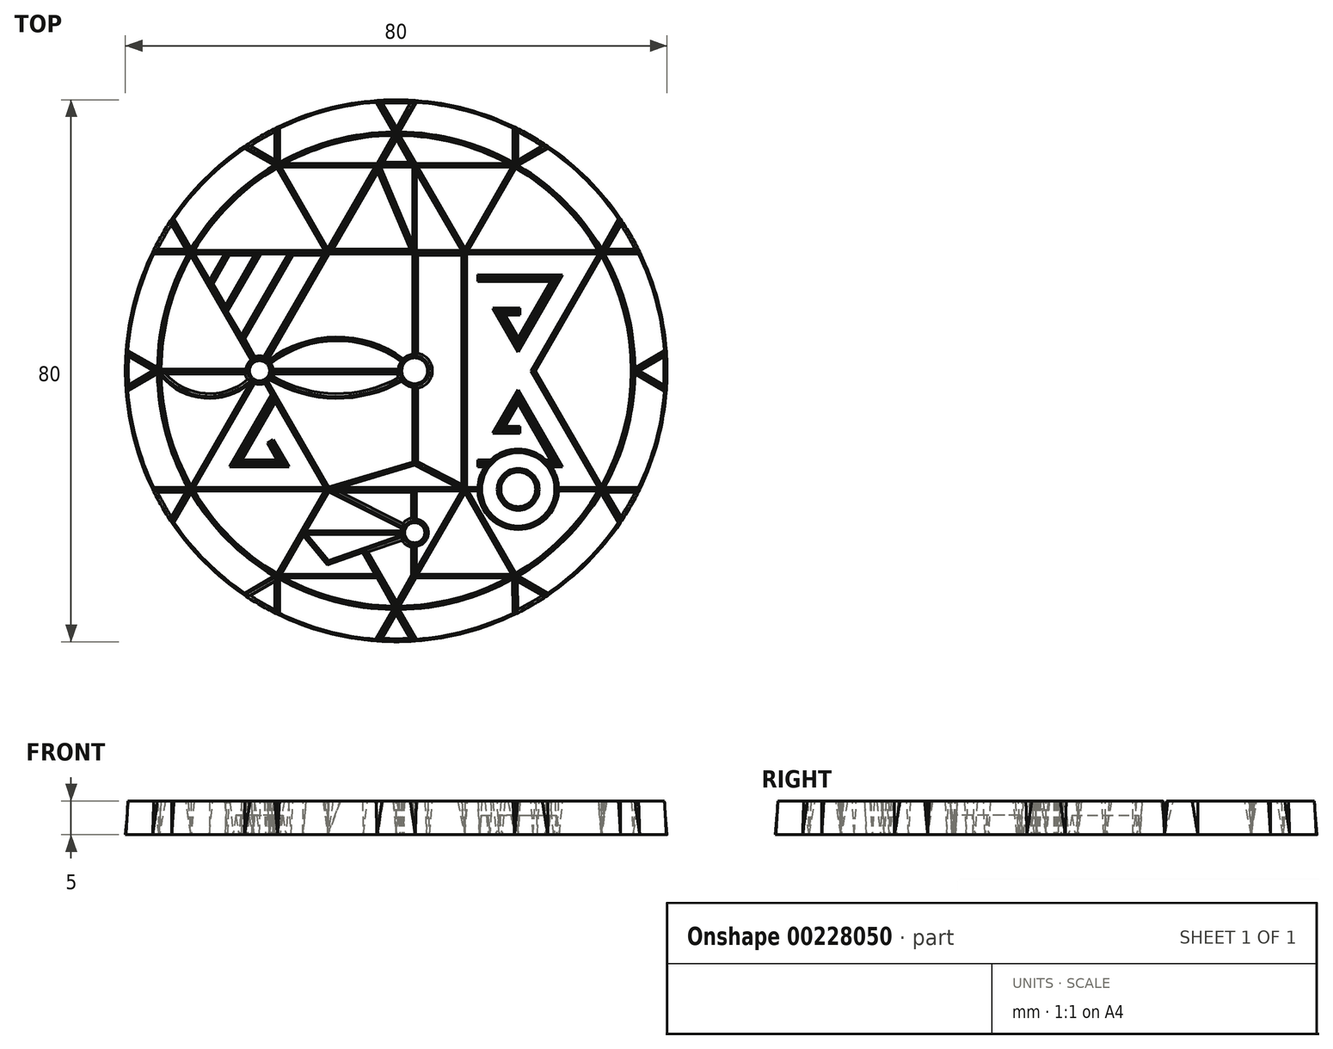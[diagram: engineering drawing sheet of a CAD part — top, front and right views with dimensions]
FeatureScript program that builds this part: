
annotation { "Feature Type Name" : "Feature", "Feature Type Description" : "" }
export const myFeature = defineFeature(function(context is Context, id is Id, definition is map)
    precondition{}
    {
        {
            var Q0;
            Q0=qCreatedBy(makeId("Top.planeOp"),FACE);
            var sketch = newSketch(context, id + "F6", { "sketchPlane" : qUnion([Q0])});
            skCircle(sketch, "E0", {"center": v(0, 0) * mm, "radius": 40 * mm});
            skCircle(sketch, "E1", {"center": v(0, 0) * mm, "radius": 35 * mm});
            skLineSegment(sketch, "E2", {"start": v(0.02, 35) * mm, "end": v(-2.82, 39.9) * mm});
            skLineSegment(sketch, "E3", {"start": v(0.02, 35) * mm, "end": v(2.83, 39.9) * mm});
            skLineSegment(sketch, "E4", {"start": v(0.02, 35) * mm, "end": v(-19.3, 1.52) * mm});
            skLineSegment(sketch, "E5", {"start": v(-30.29, -17.5) * mm, "end": v(12.34, -17.5) * mm});
            skLineSegment(sketch, "E6", {"start": v(0.02, 35) * mm, "end": v(10.12, 17.5) * mm});
            skLineSegment(sketch, "E7", {"start": v(0.02, -35) * mm, "end": v(-4.87, -26.53) * mm});
            skLineSegment(sketch, "E8", {"start": v(0.02, -35) * mm, "end": v(10.12, -17.5) * mm});
            skLineSegment(sketch, "E9", {"start": v(-30.29, 17.5) * mm, "end": v(30.33, 17.5) * mm});
            skLineSegment(sketch, "E10", {"start": v(-10.08, -17.5) * mm, "end": v(-17.48, -30.31) * mm});
            skLineSegment(sketch, "E11", {"start": v(10.12, -17.5) * mm, "end": v(17.52, -30.31) * mm});
            skLineSegment(sketch, "E12", {"start": v(17.52, -30.31) * mm, "end": v(2.73, -30.31) * mm});
            skLineSegment(sketch, "E13", {"start": v(-10.08, 17.5) * mm, "end": v(-17.48, 30.31) * mm});
            skLineSegment(sketch, "E14", {"start": v(-17.48, 30.31) * mm, "end": v(17.52, 30.31) * mm});
            skLineSegment(sketch, "E15", {"start": v(10.12, 17.5) * mm, "end": v(17.52, 30.31) * mm});
            skLineSegment(sketch, "E16", {"start": v(-24.89, 17.5) * mm, "end": v(-27.6, 12.83) * mm});
            skLineSegment(sketch, "E17", {"start": v(-20.2, 17.5) * mm, "end": v(-25.25, 8.77) * mm});
            skLineSegment(sketch, "E18", {"start": v(-15.5, 17.5) * mm, "end": v(-22.9, 4.7) * mm});
            skLineSegment(sketch, "E19", {"start": v(-30.29, -17.5) * mm, "end": v(-30.29, -17.5) * mm});
            skLineSegment(sketch, "E20", {"start": v(30.33, 17.5) * mm, "end": v(30.32, 17.5) * mm});
            skLineSegment(sketch, "E21", {"start": v(10.12, 17.5) * mm, "end": v(10.12, -17.5) * mm});
            skLineSegment(sketch, "E22.trimOffspring", {"start": v(-2.69, -30.31) * mm, "end": v(-17.48, -30.31) * mm});
            skLineSegment(sketch, "E23", {"start": v(2.73, 30.31) * mm, "end": v(2.73, 2.18) * mm});
            skLineSegment(sketch, "E24", {"start": v(-2.69, 30.31) * mm, "end": v(2.73, 17.5) * mm});
            skLineSegment(sketch, "E25.trimOffspring", {"start": v(20.23, 0) * mm, "end": v(30.33, -17.5) * mm});
            skLineSegment(sketch, "E26.trimOffspring", {"start": v(20.23, 0) * mm, "end": v(30.33, 17.5) * mm});
            skLineSegment(sketch, "E27", {"start": v(-34.98, 0) * mm, "end": v(-21.94, 0) * mm});
            skArc(sketch, "E28", {"start": v(-34.98, 0) * mm, "mid": v(-28.46, -3.76) * mm, "end": v(-21.34, -1.32) * mm});
            skArc(sketch, "E29", {"start": v(-18.73, -0.98) * mm, "mid": v(-8.94, -3.8) * mm, "end": v(0.91, -1.2) * mm});
            skArc(sketch, "E30", {"start": v(1.08, 1.42) * mm, "mid": v(-8.94, 4.7) * mm, "end": v(-18.87, 1.16) * mm});
            skLineSegment(sketch, "E31", {"start": v(-10.08, -17.5) * mm, "end": v(2.73, -13.67) * mm});
            skLineSegment(sketch, "E32", {"start": v(10.12, -17.5) * mm, "end": v(2.73, -13.67) * mm});
            skLineSegment(sketch, "E33", {"start": v(-13.78, -23.9) * mm, "end": v(0.97, -23.9) * mm});
            skLineSegment(sketch, "E34", {"start": v(1.16, -23.12) * mm, "end": v(-10.08, -17.5) * mm});
            skLineSegment(sketch, "E35", {"start": v(-13.78, -23.9) * mm, "end": v(-10.08, -28.33) * mm});
            skLineSegment(sketch, "E36", {"start": v(1.07, -24.48) * mm, "end": v(-10.08, -28.33) * mm});
            skLineSegment(sketch, "E37.trimOffspring", {"start": v(-10.08, -17.5) * mm, "end": v(-19.3, -1.52) * mm});
            skLineSegment(sketch, "E38.1.0", {"start": v(-17.48, 30.32) * mm, "end": v(-17.5, 35.97) * mm});
            skLineSegment(sketch, "E38.1.1", {"start": v(-17.48, 30.32) * mm, "end": v(-22.4, 33.14) * mm});
            skLineSegment(sketch, "E38.2.0", {"start": v(-30.3, 17.52) * mm, "end": v(-33.14, 22.4) * mm});
            skLineSegment(sketch, "E38.2.1", {"start": v(-30.3, 17.52) * mm, "end": v(-35.97, 17.5) * mm});
            skLineSegment(sketch, "E38.3.0", {"start": v(-35, 0.02) * mm, "end": v(-39.9, 2.83) * mm});
            skLineSegment(sketch, "E38.3.1", {"start": v(-35, 0.02) * mm, "end": v(-39.9, -2.82) * mm});
            skLineSegment(sketch, "E38.4.0", {"start": v(-30.32, -17.48) * mm, "end": v(-35.97, -17.5) * mm});
            skLineSegment(sketch, "E38.4.1", {"start": v(-30.32, -17.48) * mm, "end": v(-33.14, -22.4) * mm});
            skLineSegment(sketch, "E38.5.0", {"start": v(-17.52, -30.3) * mm, "end": v(-22.4, -33.14) * mm});
            skLineSegment(sketch, "E38.5.1", {"start": v(-17.52, -30.3) * mm, "end": v(-17.5, -35.97) * mm});
            skLineSegment(sketch, "E38.6.0", {"start": v(-0.02, -35) * mm, "end": v(-2.83, -39.9) * mm});
            skLineSegment(sketch, "E38.6.1", {"start": v(-0.02, -35) * mm, "end": v(2.82, -39.9) * mm});
            skLineSegment(sketch, "E38.7.0", {"start": v(17.48, -30.32) * mm, "end": v(17.5, -35.97) * mm});
            skLineSegment(sketch, "E38.7.1", {"start": v(17.48, -30.32) * mm, "end": v(22.4, -33.14) * mm});
            skLineSegment(sketch, "E38.8.0", {"start": v(30.3, -17.52) * mm, "end": v(33.14, -22.4) * mm});
            skLineSegment(sketch, "E38.8.1", {"start": v(30.3, -17.52) * mm, "end": v(35.97, -17.5) * mm});
            skLineSegment(sketch, "E38.9.0", {"start": v(35, -0.02) * mm, "end": v(39.9, -2.83) * mm});
            skLineSegment(sketch, "E38.9.1", {"start": v(35, -0.02) * mm, "end": v(39.9, 2.82) * mm});
            skLineSegment(sketch, "E38.10.0", {"start": v(30.32, 17.48) * mm, "end": v(35.97, 17.5) * mm});
            skLineSegment(sketch, "E38.10.1", {"start": v(30.32, 17.48) * mm, "end": v(33.14, 22.4) * mm});
            skLineSegment(sketch, "E38.11.0", {"start": v(17.52, 30.3) * mm, "end": v(22.4, 33.14) * mm});
            skLineSegment(sketch, "E38.11.1", {"start": v(17.52, 30.3) * mm, "end": v(17.5, 35.97) * mm});
            skCircle(sketch, "E39", {"center": v(-20.19, 0) * mm, "radius": 1.75 * mm});
            skLineSegment(sketch, "E40.trimOffspring", {"start": v(-21.06, 1.52) * mm, "end": v(-30.29, 17.5) * mm});
            skLineSegment(sketch, "E41.trimOffspring", {"start": v(-21.06, -1.52) * mm, "end": v(-30.29, -17.5) * mm});
            skLineSegment(sketch, "E42.trimOffspring", {"start": v(-18.43, 0) * mm, "end": v(0.55, 0) * mm});
            skCircle(sketch, "E43", {"center": v(2.73, 0) * mm, "radius": 2.18 * mm});
            skCircle(sketch, "E44", {"center": v(2.73, -23.9) * mm, "radius": 1.75 * mm});
            skLineSegment(sketch, "E45.trimOffspring", {"start": v(2.73, -25.66) * mm, "end": v(2.73, -30.31) * mm});
            skLineSegment(sketch, "E46.trimOffspring", {"start": v(2.73, -2.18) * mm, "end": v(2.73, -22.15) * mm});
            skPoint(sketch, "E47", {"position": v(-6.15, 0) * mm});
            skPoint(sketch, "E48", {"position": v(-2.69, 0) * mm});
            skPoint(sketch, "E49", {"position": v(-4.54, 0) * mm});
            skLineSegment(sketch, "E50", {"start": v(-34.54, -0.56) * mm, "end": v(-35.31, -1.2) * mm});
            skLineSegment(sketch, "E51.1.0", {"start": v(-33.42, -1.68) * mm, "end": v(-34.07, -2.45) * mm});
            skLineSegment(sketch, "E51.2.0", {"start": v(-32.13, -2.59) * mm, "end": v(-32.63, -3.46) * mm});
            skLineSegment(sketch, "E51.3.0", {"start": v(-30.7, -3.26) * mm, "end": v(-31.03, -4.2) * mm});
            skLineSegment(sketch, "E51.4.0", {"start": v(-29.16, -3.67) * mm, "end": v(-29.33, -4.65) * mm});
            skLineSegment(sketch, "E51.5.0", {"start": v(-27.58, -3.8) * mm, "end": v(-27.58, -4.8) * mm});
            skLineSegment(sketch, "E51.6.0", {"start": v(-26, -3.67) * mm, "end": v(-25.83, -4.65) * mm});
            skLineSegment(sketch, "E51.7.0", {"start": v(-24.47, -3.26) * mm, "end": v(-24.13, -4.2) * mm});
            skLineSegment(sketch, "E51.8.0", {"start": v(-23.04, -2.59) * mm, "end": v(-22.54, -3.46) * mm});
            skLineSegment(sketch, "E51.9.0", {"start": v(-21.74, -1.68) * mm, "end": v(-21.4, -2.1) * mm});
            skLineSegment(sketch, "E52.trimOffspring", {"start": v(-18.55, -1.1) * mm, "end": v(-19.06, -1.95) * mm});
            skLineSegment(sketch, "E53.1.0", {"start": v(-16.78, -2.03) * mm, "end": v(-17.2, -2.94) * mm});
            skLineSegment(sketch, "E53.2.0", {"start": v(-14.92, -2.78) * mm, "end": v(-15.24, -3.72) * mm});
            skLineSegment(sketch, "E53.3.0", {"start": v(-13, -3.33) * mm, "end": v(-13.22, -4.3) * mm});
            skLineSegment(sketch, "E53.4.0", {"start": v(-11.02, -3.67) * mm, "end": v(-11.14, -4.66) * mm});
            skLineSegment(sketch, "E53.5.0", {"start": v(-9.02, -3.8) * mm, "end": v(-9.04, -4.8) * mm});
            skLineSegment(sketch, "E53.6.0", {"start": v(-7.02, -3.73) * mm, "end": v(-6.93, -4.73) * mm});
            skLineSegment(sketch, "E53.7.0", {"start": v(-5.03, -3.45) * mm, "end": v(-4.84, -4.43) * mm});
            skLineSegment(sketch, "E53.8.0", {"start": v(-3.1, -2.96) * mm, "end": v(-2.8, -3.91) * mm});
            skLineSegment(sketch, "E53.9.0", {"start": v(-1.2, -2.27) * mm, "end": v(-0.82, -3.19) * mm});
            skLineSegment(sketch, "E53.10.0", {"start": v(0.59, -1.39) * mm, "end": v(1.08, -2.26) * mm});
            skCircle(sketch, "E54", {"center": v(18.02, -17.5) * mm, "radius": 5.68 * mm});
            skCircle(sketch, "E55", {"center": v(18.02, -17.5) * mm, "radius": 2.83 * mm});
            skLineSegment(sketch, "E56.trimOffspring", {"start": v(23.7, -17.5) * mm, "end": v(30.33, -17.5) * mm});
            skLineSegment(sketch, "E57.0", {"start": v(12.34, 13.42) * mm, "end": v(23.26, 13.4) * mm});
            skLineSegment(sketch, "E58.0", {"start": v(23.26, 13.4) * mm, "end": v(18.02, 4.32) * mm});
            skLineSegment(sketch, "E59.0", {"start": v(18.02, 4.32) * mm, "end": v(15.6, 8.5) * mm});
            skLineSegment(sketch, "E60.0", {"start": v(15.6, 8.5) * mm, "end": v(18.02, 8.5) * mm});
            skLineSegment(sketch, "E61.0", {"start": v(12.34, 13.92) * mm, "end": v(24.13, 13.9) * mm});
            skLineSegment(sketch, "E62.0", {"start": v(24.13, 13.9) * mm, "end": v(18.02, 3.32) * mm});
            skLineSegment(sketch, "E63.0", {"start": v(18.02, 3.32) * mm, "end": v(14.74, 9) * mm});
            skLineSegment(sketch, "E64.0", {"start": v(14.74, 9) * mm, "end": v(18.02, 9) * mm});
            skLineSegment(sketch, "E65", {"start": v(12.34, 13.92) * mm, "end": v(12.34, 13.42) * mm});
            skLineSegment(sketch, "E66", {"start": v(18.02, 9) * mm, "end": v(18.02, 8.5) * mm});
            skLineSegment(sketch, "E67.0", {"start": v(12.34, -13.92) * mm, "end": v(13.62, -13.92) * mm});
            skLineSegment(sketch, "E68.0", {"start": v(12.34, -13.42) * mm, "end": v(13.83, -13.42) * mm});
            skLineSegment(sketch, "E69", {"start": v(12.34, -13.42) * mm, "end": v(12.34, -13.92) * mm});
            skLineSegment(sketch, "E70", {"start": v(13.83, -13.42) * mm, "end": v(13.83, -13.67) * mm});
            skLineSegment(sketch, "E71.0", {"start": v(22.42, -13.9) * mm, "end": v(24.13, -13.9) * mm});
            skLineSegment(sketch, "E72.0", {"start": v(21.95, -13.4) * mm, "end": v(23.26, -13.4) * mm});
            skLineSegment(sketch, "E73.0", {"start": v(18.02, -4.32) * mm, "end": v(23.26, -13.4) * mm});
            skLineSegment(sketch, "E74.0", {"start": v(18.02, -3.32) * mm, "end": v(24.13, -13.9) * mm});
            skLineSegment(sketch, "E75.0", {"start": v(18.02, -3.32) * mm, "end": v(14.74, -9) * mm});
            skLineSegment(sketch, "E76.0", {"start": v(18.02, -4.32) * mm, "end": v(15.6, -8.5) * mm});
            skLineSegment(sketch, "E77.0", {"start": v(14.74, -9) * mm, "end": v(18.02, -9) * mm});
            skLineSegment(sketch, "E78.0", {"start": v(15.6, -8.5) * mm, "end": v(18.02, -8.5) * mm});
            skLineSegment(sketch, "E79", {"start": v(18.02, -8.5) * mm, "end": v(18.02, -9) * mm});
            skLineSegment(sketch, "E80.0", {"start": v(-18.13, -3.56) * mm, "end": v(-24.1, -13.9) * mm});
            skLineSegment(sketch, "E81.0", {"start": v(-17.84, -4.06) * mm, "end": v(-23.24, -13.4) * mm});
            skLineSegment(sketch, "E82.0", {"start": v(-24.1, -13.9) * mm, "end": v(-16.3, -13.91) * mm});
            skLineSegment(sketch, "E83.0", {"start": v(-23.24, -13.4) * mm, "end": v(-17.16, -13.4) * mm});
            skLineSegment(sketch, "E84.0", {"start": v(-16.3, -13.91) * mm, "end": v(-18.24, -10.53) * mm});
            skLineSegment(sketch, "E85.0", {"start": v(-17.16, -13.4) * mm, "end": v(-18.68, -10.77) * mm});
            skLineSegment(sketch, "E86", {"start": v(-18.24, -10.53) * mm, "end": v(-18.68, -10.77) * mm});
            skSolve(sketch);
        }
        {
            var Q0;
            {var subQ0=sQuery(id+"F6.wireOp",EDGE,"E38.1.0");Q0=makeQuery(id+"F6.imprint","IMPRINT",FACE,{"disambiguationData":[TD([[makeQuery(id+"F6.imprint","IMPRINT",EDGE,{"derivedFrom":subQ0}),1.0]])]});}
            var Q1;
            {var subQ0=sQuery(id+"F6.wireOp",EDGE,"E2");Q1=makeQuery(id+"F6.imprint","IMPRINT",FACE,{"disambiguationData":[TD([[makeQuery(id+"F6.imprint","IMPRINT",EDGE,{"derivedFrom":subQ0}),-1.0]])]});}
            var Q2;
            {var subQ1=sQuery(id+"F6.wireOp",EDGE,"E38.11.0");Q2=makeQuery(id+"F6.imprint","IMPRINT",FACE,{"disambiguationData":[TD([[makeQuery(id+"F6.imprint","IMPRINT",EDGE,{"derivedFrom":subQ1}),1.0]])]});}
            var Q3;
            {var subQ3=sQuery(id+"F6.wireOp",EDGE,"E38.10.0");Q3=makeQuery(id+"F6.imprint","IMPRINT",FACE,{"disambiguationData":[TD([[makeQuery(id+"F6.imprint","IMPRINT",EDGE,{"derivedFrom":subQ3}),1.0]])]});}
            var Q4;
            {var subQ0=sQuery(id+"F6.wireOp",EDGE,"E38.9.0");Q4=makeQuery(id+"F6.imprint","IMPRINT",FACE,{"disambiguationData":[TD([[makeQuery(id+"F6.imprint","IMPRINT",EDGE,{"derivedFrom":subQ0}),1.0]])]});}
            var Q5;
            {var subQ0=sQuery(id+"F6.wireOp",EDGE,"E38.8.0");Q5=makeQuery(id+"F6.imprint","IMPRINT",FACE,{"disambiguationData":[TD([[makeQuery(id+"F6.imprint","IMPRINT",EDGE,{"derivedFrom":subQ0}),1.0]])]});}
            var Q6;
            {var subQ0=sQuery(id+"F6.wireOp",EDGE,"E38.7.0");Q6=makeQuery(id+"F6.imprint","IMPRINT",FACE,{"disambiguationData":[TD([[makeQuery(id+"F6.imprint","IMPRINT",EDGE,{"derivedFrom":subQ0}),1.0]])]});}
            var Q7;
            {var subQ0=sQuery(id+"F6.wireOp",EDGE,"E38.6.0");Q7=makeQuery(id+"F6.imprint","IMPRINT",FACE,{"disambiguationData":[TD([[makeQuery(id+"F6.imprint","IMPRINT",EDGE,{"derivedFrom":subQ0}),1.0]])]});}
            var Q8;
            {var subQ0=sQuery(id+"F6.wireOp",EDGE,"E38.5.0");Q8=makeQuery(id+"F6.imprint","IMPRINT",FACE,{"disambiguationData":[TD([[makeQuery(id+"F6.imprint","IMPRINT",EDGE,{"derivedFrom":subQ0}),1.0]])]});}
            var Q9;
            {var subQ0=sQuery(id+"F6.wireOp",EDGE,"E38.4.0");Q9=makeQuery(id+"F6.imprint","IMPRINT",FACE,{"disambiguationData":[TD([[makeQuery(id+"F6.imprint","IMPRINT",EDGE,{"derivedFrom":subQ0}),1.0]])]});}
            var Q10;
            {var subQ0=sQuery(id+"F6.wireOp",EDGE,"E38.3.0");Q10=makeQuery(id+"F6.imprint","IMPRINT",FACE,{"disambiguationData":[TD([[makeQuery(id+"F6.imprint","IMPRINT",EDGE,{"derivedFrom":subQ0}),1.0]])]});}
            var Q11;
            {var subQ0=sQuery(id+"F6.wireOp",EDGE,"E38.2.0");Q11=makeQuery(id+"F6.imprint","IMPRINT",FACE,{"disambiguationData":[TD([[makeQuery(id+"F6.imprint","IMPRINT",EDGE,{"derivedFrom":subQ0}),1.0]])]});}
            var Q12;
            {var subQ3=sQuery(id+"F6.wireOp",EDGE,"E27");Q12=makeQuery(id+"F6.imprint","IMPRINT",FACE,{"disambiguationData":[TD([[makeQuery(id+"F6.imprint","IMPRINT",EDGE,{"derivedFrom":subQ3}),-1.0]])]});}
            var Q13;
            {var subQ16=sQuery(id+"F6.wireOp",EDGE,"E42.trimOffspring");Q13=makeQuery(id+"F6.imprint","IMPRINT",FACE,{"disambiguationData":[TD([[makeQuery(id+"F6.imprint","IMPRINT",EDGE,{"derivedFrom":subQ16}),-1.0]])]});}
            var Q14;
            {var subQ1=sQuery(id+"F6.wireOp",EDGE,"E37.trimOffspring");var subQ4=makeQuery(id+"F6.imprint","IMPRINT",VERTEX,{"derivedFrom":subQ1});Q14=makeQuery(id+"F6.imprint","IMPRINT",FACE,{"disambiguationData":[TD([[makeQuery(id+"F6.imprint","IMPRINT",EDGE,{"disambiguationData":[TD([[subQ4,-1.0]])],"derivedFrom":subQ1}),1.0]])]});}
            var Q15;
            {var subQ0=sQuery(id+"F6.wireOp",EDGE,"E16");Q15=makeQuery(id+"F6.imprint","IMPRINT",FACE,{"disambiguationData":[TD([[makeQuery(id+"F6.imprint","IMPRINT",EDGE,{"derivedFrom":subQ0}),1.0]])]});}
            var Q16;
            {var subQ5=sQuery(id+"F6.wireOp",EDGE,"E18");Q16=makeQuery(id+"F6.imprint","IMPRINT",FACE,{"disambiguationData":[TD([[makeQuery(id+"F6.imprint","IMPRINT",EDGE,{"derivedFrom":subQ5}),1.0]])]});}
            var Q17;
            {var subQ3=sQuery(id+"F6.wireOp",EDGE,"E24");Q17=makeQuery(id+"F6.imprint","IMPRINT",FACE,{"disambiguationData":[TD([[makeQuery(id+"F6.imprint","IMPRINT",EDGE,{"derivedFrom":subQ3}),-1.0]])]});}
            var Q18;
            {var subQ0=sQuery(id+"F6.wireOp",EDGE,"E6");var subQ3=sQuery(id+"F6.wireOp",EDGE,"E14");var subQ5=makeQuery(id+"F6.imprint","INTERSECT",VERTEX,{"derivedFrom":[subQ0,subQ3,sQuery(id+"F6.wireOp",EDGE,"E23")]});Q18=makeQuery(id+"F6.imprint","IMPRINT",FACE,{"disambiguationData":[TD([[makeQuery(id+"F6.imprint","IMPRINT",EDGE,{"disambiguationData":[TD([[subQ5,1.0]])],"derivedFrom":subQ3}),1.0]])]});}
            var Q19;
            {var subQ8=sQuery(id+"F6.wireOp",EDGE,"E21");Q19=makeQuery(id+"F6.imprint","IMPRINT",FACE,{"disambiguationData":[TD([[makeQuery(id+"F6.imprint","IMPRINT",EDGE,{"derivedFrom":subQ8}),-1.0]])]});}
            var Q20;
            {var subQ0=sQuery(id+"F6.wireOp",EDGE,"E34");Q20=makeQuery(id+"F6.imprint","IMPRINT",FACE,{"disambiguationData":[TD([[makeQuery(id+"F6.imprint","IMPRINT",EDGE,{"derivedFrom":subQ0}),-1.0]])]});}
            var Q21;
            {var subQ6=sQuery(id+"F6.wireOp",EDGE,"E45.trimOffspring");Q21=makeQuery(id+"F6.imprint","IMPRINT",FACE,{"disambiguationData":[TD([[makeQuery(id+"F6.imprint","IMPRINT",EDGE,{"derivedFrom":subQ6}),-1.0]])]});}
            var Q22;
            {var subQ0=sQuery(id+"F6.wireOp",EDGE,"39669ad0-43e0-4bce-9135-b1033924fe43.trimOffspring");Q22=makeQuery(id+"F6.imprint","IMPRINT",FACE,{"disambiguationData":[TD([[makeQuery(id+"F6.imprint","IMPRINT",EDGE,{"derivedFrom":subQ0}),1.0]])]});}
            var Q23;
            {var subQ0=sQuery(id+"F6.wireOp",EDGE,"39669ad0-43e0-4bce-9135-b1033924fe43.trimOffspring");Q23=makeQuery(id+"F6.imprint","IMPRINT",FACE,{"disambiguationData":[TD([[makeQuery(id+"F6.imprint","IMPRINT",EDGE,{"derivedFrom":subQ0}),-1.0]])]});}
            var Q24;
            {var subQ1=sQuery(id+"F6.wireOp",EDGE,"E80.0");Q24=makeQuery(id+"F6.imprint","IMPRINT",FACE,{"disambiguationData":[TD([[makeQuery(id+"F6.imprint","IMPRINT",EDGE,{"derivedFrom":subQ1}),1.0]])]});}
            var Q25;
            {var subQ0=sQuery(id+"F6.wireOp",EDGE,"E67.0");Q25=makeQuery(id+"F6.imprint","IMPRINT",FACE,{"disambiguationData":[TD([[makeQuery(id+"F6.imprint","IMPRINT",EDGE,{"derivedFrom":subQ0}),1.0]])]});}
            var Q26;
            {var subQ0=sQuery(id+"F6.wireOp",EDGE,"E71.0");Q26=makeQuery(id+"F6.imprint","IMPRINT",FACE,{"disambiguationData":[TD([[makeQuery(id+"F6.imprint","IMPRINT",EDGE,{"derivedFrom":subQ0}),1.0]])]});}
            var Q27;
            Q27=makeQuery(id+"F6.imprint","IMPRINT",FACE,{"disambiguationData":[TD([[makeQuery(id+"F6.imprint","IMPRINT",EDGE,{"derivedFrom":sQuery(id+"F6.wireOp",EDGE,"E57.0")}),1.0]])]});
            extrude(context, id + "F0", {"entities" : qUnion([Q0, Q1, Q2, Q3, Q4, Q5, Q6, Q7, Q8, Q9, Q10, Q11, Q12, Q13, Q14, Q15, Q16, Q17, Q18, Q19, Q20, Q21, Q22, Q23, Q24, Q25, Q26, Q27]), "depth" : 5 * mm, "hasDraft" : true, "draftAngle" : 5 * degree, "draftPullDirection" : true});
        }
        {
            var Q0;
            {var subQ0=sQuery(id+"F6.wireOp",EDGE,"E2");Q0=makeQuery(id+"F6.imprint","IMPRINT",FACE,{"disambiguationData":[TD([[makeQuery(id+"F6.imprint","IMPRINT",EDGE,{"derivedFrom":subQ0}),1.0]])]});}
            var Q1;
            {var subQ0=sQuery(id+"F6.wireOp",EDGE,"E38.1.1");Q1=makeQuery(id+"F6.imprint","IMPRINT",FACE,{"disambiguationData":[TD([[makeQuery(id+"F6.imprint","IMPRINT",EDGE,{"derivedFrom":subQ0}),1.0]])]});}
            var Q2;
            {var subQ0=sQuery(id+"F6.wireOp",EDGE,"E38.2.1");Q2=makeQuery(id+"F6.imprint","IMPRINT",FACE,{"disambiguationData":[TD([[makeQuery(id+"F6.imprint","IMPRINT",EDGE,{"derivedFrom":subQ0}),1.0]])]});}
            var Q3;
            {var subQ1=sQuery(id+"F6.wireOp",EDGE,"E38.3.1");Q3=makeQuery(id+"F6.imprint","IMPRINT",FACE,{"disambiguationData":[TD([[makeQuery(id+"F6.imprint","IMPRINT",EDGE,{"derivedFrom":subQ1}),1.0]])]});}
            var Q4;
            {var subQ0=sQuery(id+"F6.wireOp",EDGE,"E38.4.1");Q4=makeQuery(id+"F6.imprint","IMPRINT",FACE,{"disambiguationData":[TD([[makeQuery(id+"F6.imprint","IMPRINT",EDGE,{"derivedFrom":subQ0}),1.0]])]});}
            var Q5;
            {var subQ0=sQuery(id+"F6.wireOp",EDGE,"E38.5.1");Q5=makeQuery(id+"F6.imprint","IMPRINT",FACE,{"disambiguationData":[TD([[makeQuery(id+"F6.imprint","IMPRINT",EDGE,{"derivedFrom":subQ0}),1.0]])]});}
            var Q6;
            {var subQ1=sQuery(id+"F6.wireOp",EDGE,"E38.6.1");Q6=makeQuery(id+"F6.imprint","IMPRINT",FACE,{"disambiguationData":[TD([[makeQuery(id+"F6.imprint","IMPRINT",EDGE,{"derivedFrom":subQ1}),1.0]])]});}
            var Q7;
            {var subQ6=sQuery(id+"F6.wireOp",EDGE,"E38.7.1");Q7=makeQuery(id+"F6.imprint","IMPRINT",FACE,{"disambiguationData":[TD([[makeQuery(id+"F6.imprint","IMPRINT",EDGE,{"derivedFrom":subQ6}),1.0]])]});}
            var Q8;
            {var subQ5=sQuery(id+"F6.wireOp",EDGE,"E38.8.1");Q8=makeQuery(id+"F6.imprint","IMPRINT",FACE,{"disambiguationData":[TD([[makeQuery(id+"F6.imprint","IMPRINT",EDGE,{"derivedFrom":subQ5}),1.0]])]});}
            var Q9;
            {var subQ0=sQuery(id+"F6.wireOp",EDGE,"E38.9.1");Q9=makeQuery(id+"F6.imprint","IMPRINT",FACE,{"disambiguationData":[TD([[makeQuery(id+"F6.imprint","IMPRINT",EDGE,{"derivedFrom":subQ0}),1.0]])]});}
            var Q10;
            {var subQ5=sQuery(id+"F6.wireOp",EDGE,"E38.11.0");Q10=makeQuery(id+"F6.imprint","IMPRINT",FACE,{"disambiguationData":[TD([[makeQuery(id+"F6.imprint","IMPRINT",EDGE,{"derivedFrom":subQ5}),-1.0]])]});}
            var Q11;
            {var subQ5=sQuery(id+"F6.wireOp",EDGE,"E3");Q11=makeQuery(id+"F6.imprint","IMPRINT",FACE,{"disambiguationData":[TD([[makeQuery(id+"F6.imprint","IMPRINT",EDGE,{"derivedFrom":subQ5}),-1.0]])]});}
            var Q12;
            {var subQ0=sQuery(id+"F6.wireOp",EDGE,"E13");Q12=makeQuery(id+"F6.imprint","IMPRINT",FACE,{"disambiguationData":[TD([[makeQuery(id+"F6.imprint","IMPRINT",EDGE,{"derivedFrom":subQ0}),-1.0]])]});}
            var Q13;
            {var subQ0=sQuery(id+"F6.wireOp",EDGE,"E15");var subQ1=sQuery(id+"F6.wireOp",EDGE,"E1");var subQ2=makeQuery(id+"F6.imprint","INTERSECT",VERTEX,{"derivedFrom":[subQ1,subQ0]});Q13=makeQuery(id+"F6.imprint","IMPRINT",FACE,{"disambiguationData":[TD([[makeQuery(id+"F6.imprint","IMPRINT",EDGE,{"disambiguationData":[TD([[subQ2,-1.0]])],"derivedFrom":subQ1}),1.0]])]});}
            var Q14;
            {var subQ3=sQuery(id+"F6.wireOp",EDGE,"E24");Q14=makeQuery(id+"F6.imprint","IMPRINT",FACE,{"disambiguationData":[TD([[makeQuery(id+"F6.imprint","IMPRINT",EDGE,{"derivedFrom":subQ3}),1.0]])]});}
            var Q15;
            {var subQ0=sQuery(id+"F6.wireOp",EDGE,"E39");var subQ4=makeQuery(id+"F6.imprint","INTERSECT",VERTEX,{"derivedFrom":[sQuery(id+"F6.wireOp",EDGE,"E30"),subQ0]});Q15=makeQuery(id+"F6.imprint","IMPRINT",FACE,{"disambiguationData":[TD([[makeQuery(id+"F6.imprint","IMPRINT",EDGE,{"disambiguationData":[TD([[subQ4,1.0]])],"derivedFrom":subQ0}),1.0]])]});}
            var Q16;
            {var subQ0=sQuery(id+"F6.wireOp",EDGE,"E43");var subQ5=makeQuery(id+"F6.imprint","INTERSECT",VERTEX,{"derivedFrom":[sQuery(id+"F6.wireOp",EDGE,"E23"),subQ0]});Q16=makeQuery(id+"F6.imprint","IMPRINT",FACE,{"disambiguationData":[TD([[makeQuery(id+"F6.imprint","IMPRINT",EDGE,{"disambiguationData":[TD([[subQ5,-1.0]])],"derivedFrom":subQ0}),1.0]])]});}
            var Q17;
            {var subQ0=sQuery(id+"F6.wireOp",EDGE,"E31");Q17=makeQuery(id+"F6.imprint","IMPRINT",FACE,{"disambiguationData":[TD([[makeQuery(id+"F6.imprint","IMPRINT",EDGE,{"derivedFrom":subQ0}),-1.0]])]});}
            var Q18;
            {var subQ0=sQuery(id+"F6.wireOp",EDGE,"E32");Q18=makeQuery(id+"F6.imprint","IMPRINT",FACE,{"disambiguationData":[TD([[makeQuery(id+"F6.imprint","IMPRINT",EDGE,{"derivedFrom":subQ0}),1.0]])]});}
            var Q19;
            {var subQ0=sQuery(id+"F6.wireOp",EDGE,"E22.trimOffspring");Q19=makeQuery(id+"F6.imprint","IMPRINT",FACE,{"disambiguationData":[TD([[makeQuery(id+"F6.imprint","IMPRINT",EDGE,{"derivedFrom":subQ0}),-1.0]])]});}
            var Q20;
            {var subQ0=sQuery(id+"F6.wireOp",EDGE,"E12");var subQ1=sQuery(id+"F6.wireOp",EDGE,"E1");var subQ2=makeQuery(id+"F6.imprint","INTERSECT",VERTEX,{"derivedFrom":[subQ1,subQ0]});Q20=makeQuery(id+"F6.imprint","IMPRINT",FACE,{"disambiguationData":[TD([[makeQuery(id+"F6.imprint","IMPRINT",EDGE,{"disambiguationData":[TD([[subQ2,-1.0]])],"derivedFrom":subQ1}),1.0]])]});}
            var Q21;
            {var subQ0=sQuery(id+"F6.wireOp",EDGE,"E44");var subQ4=makeQuery(id+"F6.imprint","INTERSECT",VERTEX,{"derivedFrom":[sQuery(id+"F6.wireOp",EDGE,"E34"),subQ0]});Q21=makeQuery(id+"F6.imprint","IMPRINT",FACE,{"disambiguationData":[TD([[makeQuery(id+"F6.imprint","IMPRINT",EDGE,{"disambiguationData":[TD([[subQ4,1.0]])],"derivedFrom":subQ0}),1.0]])]});}
            var Q22;
            Q22=makeQuery(id+"F6.imprint","IMPRINT",FACE,{"disambiguationData":[TD([[makeQuery(id+"F6.imprint","IMPRINT",EDGE,{"derivedFrom":sQuery(id+"F6.wireOp",EDGE,"E55")}),-1.0]])]});
            extrude(context, id + "F1", {"entities" : qUnion([Q0, Q1, Q2, Q3, Q4, Q5, Q6, Q7, Q8, Q9, Q10, Q11, Q12, Q13, Q14, Q15, Q16, Q17, Q18, Q19, Q20, Q21, Q22]), "depth" : 5 * mm, "hasDraft" : true, "draftAngle" : 3 * degree, "draftPullDirection" : true});
        }
        {
            var Q0;
            {var subQ0=sQuery(id+"F6.wireOp",EDGE,"E13");Q0=makeQuery(id+"F6.imprint","IMPRINT",FACE,{"disambiguationData":[TD([[makeQuery(id+"F6.imprint","IMPRINT",EDGE,{"derivedFrom":subQ0}),1.0]])]});}
            var Q1;
            {var subQ1=sQuery(id+"F6.wireOp",EDGE,"E1");var subQ3=sQuery(id+"F6.wireOp",EDGE,"E14");var subQ4=makeQuery(id+"F6.imprint","INTERSECT",VERTEX,{"derivedFrom":[subQ1,subQ3]});Q1=makeQuery(id+"F6.imprint","IMPRINT",FACE,{"disambiguationData":[TD([[makeQuery(id+"F6.imprint","IMPRINT",EDGE,{"disambiguationData":[TD([[subQ4,1.0]])],"derivedFrom":subQ3}),1.0]])]});}
            var Q2;
            {var subQ0=sQuery(id+"F6.wireOp",EDGE,"E1");var subQ2=sQuery(id+"F6.wireOp",EDGE,"E9");var subQ3=makeQuery(id+"F6.imprint","INTERSECT",VERTEX,{"derivedFrom":[subQ0,subQ2]});Q2=makeQuery(id+"F6.imprint","IMPRINT",FACE,{"disambiguationData":[TD([[makeQuery(id+"F6.imprint","IMPRINT",EDGE,{"disambiguationData":[TD([[subQ3,-1.0]])],"derivedFrom":subQ0}),1.0]])]});}
            var Q3;
            {var subQ2=sQuery(id+"F6.wireOp",EDGE,"E25.trimOffspring");var subQ4=sQuery(id+"F6.wireOp",EDGE,"E26.trimOffspring");var subQ6=makeQuery(id+"F6.imprint","INTERSECT",VERTEX,{"derivedFrom":[subQ2,subQ4]});Q3=makeQuery(id+"F6.imprint","IMPRINT",FACE,{"disambiguationData":[TD([[makeQuery(id+"F6.imprint","IMPRINT",EDGE,{"disambiguationData":[TD([[subQ6,-1.0]])],"derivedFrom":subQ2}),1.0]])]});}
            var Q4;
            {var subQ0=sQuery(id+"F6.wireOp",EDGE,"E1");var subQ2=sQuery(id+"F6.wireOp",EDGE,"E11");var subQ3=makeQuery(id+"F6.imprint","INTERSECT",VERTEX,{"derivedFrom":[subQ0,subQ2]});Q4=makeQuery(id+"F6.imprint","IMPRINT",FACE,{"disambiguationData":[TD([[makeQuery(id+"F6.imprint","IMPRINT",EDGE,{"disambiguationData":[TD([[subQ3,-1.0]])],"derivedFrom":subQ0}),1.0]])]});}
            var Q5;
            {var subQ1=sQuery(id+"F6.wireOp",EDGE,"E1");var subQ4=sQuery(id+"F6.wireOp",EDGE,"E12");var subQ5=makeQuery(id+"F6.imprint","INTERSECT",VERTEX,{"derivedFrom":[subQ1,subQ4]});Q5=makeQuery(id+"F6.imprint","IMPRINT",FACE,{"disambiguationData":[TD([[makeQuery(id+"F6.imprint","IMPRINT",EDGE,{"disambiguationData":[TD([[subQ5,1.0]])],"derivedFrom":subQ1}),1.0]])]});}
            var Q6;
            {var subQ0=sQuery(id+"F6.wireOp",EDGE,"E22.trimOffspring");Q6=makeQuery(id+"F6.imprint","IMPRINT",FACE,{"disambiguationData":[TD([[makeQuery(id+"F6.imprint","IMPRINT",EDGE,{"derivedFrom":subQ0}),1.0]])]});}
            var Q7;
            {var subQ3=sQuery(id+"F6.wireOp",EDGE,"E51.9.0");Q7=makeQuery(id+"F6.imprint","IMPRINT",FACE,{"disambiguationData":[TD([[makeQuery(id+"F6.imprint","IMPRINT",EDGE,{"derivedFrom":subQ3}),1.0]])]});}
            extrude(context, id + "F2", {"entities" : qUnion([Q0, Q1, Q2, Q3, Q4, Q5, Q6, Q7]), "depth" : 5 * mm, "hasDraft" : true, "draftAngle" : 3 * degree, "draftPullDirection" : true});
        }
        {
            var Q0;
            {var subQ3=sQuery(id+"F6.wireOp",EDGE,"E16");Q0=makeQuery(id+"F6.imprint","IMPRINT",FACE,{"disambiguationData":[TD([[makeQuery(id+"F6.imprint","IMPRINT",EDGE,{"derivedFrom":subQ3}),-1.0]])]});}
            var Q1;
            {var subQ0=sQuery(id+"F6.wireOp",EDGE,"E17");Q1=makeQuery(id+"F6.imprint","IMPRINT",FACE,{"disambiguationData":[TD([[makeQuery(id+"F6.imprint","IMPRINT",EDGE,{"derivedFrom":subQ0}),1.0]])]});}
            var Q2;
            {var subQ0=sQuery(id+"F6.wireOp",EDGE,"E30");Q2=makeQuery(id+"F6.imprint","IMPRINT",FACE,{"disambiguationData":[TD([[makeQuery(id+"F6.imprint","IMPRINT",EDGE,{"derivedFrom":subQ0}),-1.0]])]});}
            var Q3;
            {var subQ1=sQuery(id+"F6.wireOp",EDGE,"E6");var subQ3=sQuery(id+"F6.wireOp",EDGE,"E23");var subQ4=makeQuery(id+"F6.imprint","INTERSECT",VERTEX,{"derivedFrom":[subQ1,sQuery(id+"F6.wireOp",EDGE,"E14"),subQ3]});Q3=makeQuery(id+"F6.imprint","IMPRINT",FACE,{"disambiguationData":[TD([[makeQuery(id+"F6.imprint","IMPRINT",EDGE,{"disambiguationData":[TD([[subQ4,-1.0]])],"derivedFrom":subQ3}),1.0]])]});}
            var Q4;
            {var subQ15=sQuery(id+"F6.wireOp",EDGE,"E31");Q4=makeQuery(id+"F6.imprint","IMPRINT",FACE,{"disambiguationData":[TD([[makeQuery(id+"F6.imprint","IMPRINT",EDGE,{"derivedFrom":subQ15}),1.0]])]});}
            var Q5;
            {var subQ2=sQuery(id+"F6.wireOp",EDGE,"E33");Q5=makeQuery(id+"F6.imprint","IMPRINT",FACE,{"disambiguationData":[TD([[makeQuery(id+"F6.imprint","IMPRINT",EDGE,{"derivedFrom":subQ2}),1.0]])]});}
            var Q6;
            {var subQ0=sQuery(id+"F6.wireOp",EDGE,"E45.trimOffspring");Q6=makeQuery(id+"F6.imprint","IMPRINT",FACE,{"disambiguationData":[TD([[makeQuery(id+"F6.imprint","IMPRINT",EDGE,{"derivedFrom":subQ0}),1.0]])]});}
            var Q7;
            {var subQ0=sQuery(id+"F6.wireOp",EDGE,"E39");var subQ1=sQuery(id+"F6.wireOp",EDGE,"E29");var subQ2=makeQuery(id+"F6.imprint","INTERSECT",VERTEX,{"derivedFrom":[subQ1,subQ0]});Q7=makeQuery(id+"F6.imprint","IMPRINT",FACE,{"disambiguationData":[TD([[makeQuery(id+"F6.imprint","IMPRINT",EDGE,{"disambiguationData":[TD([[subQ2,-1.0]])],"derivedFrom":subQ1}),-1.0]])]});}
            extrude(context, id + "F3", {"entities" : qUnion([Q0, Q1, Q2, Q3, Q4, Q5, Q6, Q7]), "depth" : 5 * mm, "hasDraft" : true, "draftAngle" : 3 * degree, "draftPullDirection" : true});
        }
        {
            var Q0;
            {var subQ0=sQuery(id+"F6.wireOp",EDGE,"E30");Q0=makeQuery(id+"F6.imprint","IMPRINT",FACE,{"disambiguationData":[TD([[makeQuery(id+"F6.imprint","IMPRINT",EDGE,{"derivedFrom":subQ0}),1.0]])]});}
            var Q1;
            {var subQ5=sQuery(id+"F6.wireOp",EDGE,"E33");Q1=makeQuery(id+"F6.imprint","IMPRINT",FACE,{"disambiguationData":[TD([[makeQuery(id+"F6.imprint","IMPRINT",EDGE,{"derivedFrom":subQ5}),-1.0]])]});}
            extrude(context, id + "F4", {"entities" : qUnion([Q0, Q1]), "depth" : 5 * mm, "hasDraft" : true, "draftAngle" : 3 * degree, "draftPullDirection" : true});
        }
        {
            var Q0;
            {var subQ0=sQuery(id+"F6.wireOp",EDGE,"E54");var subQ3=makeQuery(id+"F6.imprint","IMPRINT",VERTEX,{"disambiguationData":[OD(0.0)],"derivedFrom":subQ0});Q0=makeQuery(id+"F6.imprint","IMPRINT",FACE,{"disambiguationData":[TD([[makeQuery(id+"F6.imprint","IMPRINT",EDGE,{"disambiguationData":[TD([[subQ3,1.0]])],"derivedFrom":subQ0}),1.0]])]});}
            var Q1;
            Q1=makeQuery(id+"F6.imprint","IMPRINT",FACE,{"disambiguationData":[TD([[makeQuery(id+"F6.imprint","IMPRINT",EDGE,{"derivedFrom":sQuery(id+"F6.wireOp",EDGE,"E55")}),1.0]])]});
            var Q2;
            {var subQ0=sQuery(id+"F6.wireOp",EDGE,"E80.0");Q2=makeQuery(id+"F6.imprint","IMPRINT",FACE,{"disambiguationData":[TD([[makeQuery(id+"F6.imprint","IMPRINT",EDGE,{"derivedFrom":subQ0}),-1.0]])]});}
            extrude(context, id + "F5", {"entities" : qUnion([Q0, Q1, Q2]), "depth" : 5 * mm, "hasDraft" : true, "draftAngle" : 3 * degree, "draftPullDirection" : true});
        }
        {
            var Q0;
            {var subQ13=sQuery(id+"F6.wireOp",EDGE,"E21");Q0=makeQuery(id+"F6.imprint","IMPRINT",FACE,{"disambiguationData":[TD([[makeQuery(id+"F6.imprint","IMPRINT",EDGE,{"derivedFrom":subQ13}),1.0]])]});}
            extrude(context, id + "F7", {"entities" : qUnion([Q0]), "depth" : 5 * mm, "hasDraft" : true, "draftAngle" : 3 * degree, "draftPullDirection" : true});
        }
    });
